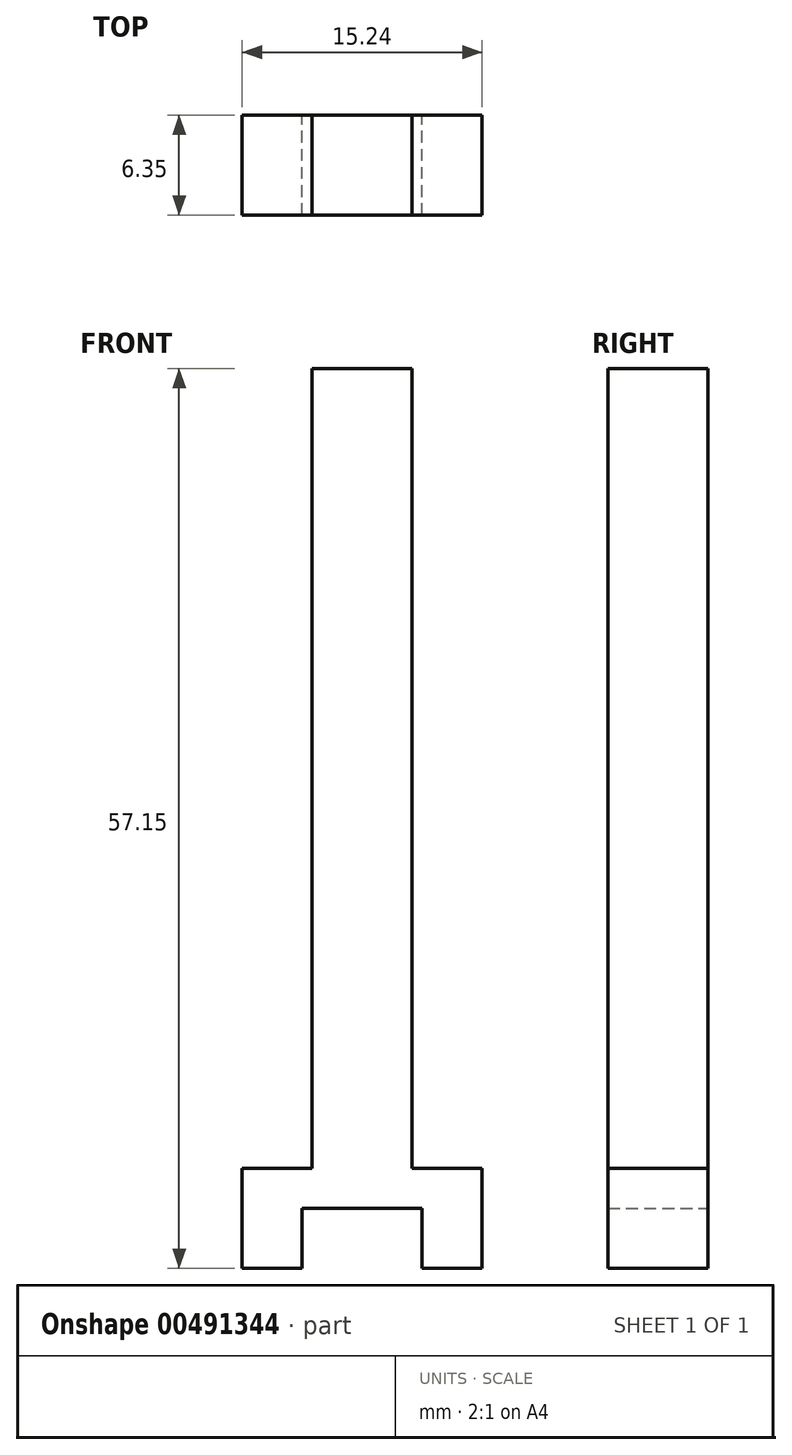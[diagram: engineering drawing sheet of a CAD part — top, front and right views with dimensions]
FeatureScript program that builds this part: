
annotation { "Feature Type Name" : "Feature", "Feature Type Description" : "" }
export const myFeature = defineFeature(function(context is Context, id is Id, definition is map)
    precondition{}
    {
        {
            var Q0;
            Q0=qCreatedBy(makeId("Front.planeOp"),FACE);
            var sketch = newSketch(context, id + "F0", { "sketchPlane" : qUnion([Q0])});
            skLineSegment(sketch, "E0.bottom", {"start": v(0, 0) * mm, "end": v(15.24, 0) * mm});
            skLineSegment(sketch, "E0.top", {"start": v(0, 6.35) * mm, "end": v(15.24, 6.35) * mm});
            skLineSegment(sketch, "E0.left", {"start": v(0, 0) * mm, "end": v(0, 6.35) * mm});
            skLineSegment(sketch, "E0.right", {"start": v(15.24, 0) * mm, "end": v(15.24, 6.35) * mm});
            skLineSegment(sketch, "E1.bottom", {"start": v(3.81, 0) * mm, "end": v(11.43, 0) * mm});
            skLineSegment(sketch, "E1.top", {"start": v(3.8, 3.81) * mm, "end": v(11.43, 3.81) * mm});
            skLineSegment(sketch, "E1.left", {"start": v(3.81, 0) * mm, "end": v(3.8, 3.8) * mm});
            skLineSegment(sketch, "E1.right", {"start": v(11.43, 0) * mm, "end": v(11.43, 3.8) * mm});
            skSolve(sketch);
        }
        {
            var Q0;
            Q0=makeQuery(id+"F0.imprint","IMPRINT",FACE,{"disambiguationData":[TD([[makeQuery(id+"F0.imprint","IMPRINT",EDGE,{"derivedFrom":sQuery(id+"F0.wireOp",EDGE,"E0.top")}),-1.0]])]});
            extrude(context, id + "F1", {"entities" : qUnion([Q0]), "depth" : 6.35 * mm});
        }
        {
            var Q0;
            Q0=makeQuery(id+"F1.opExtrude","SWEPT_FACE",FACE,{"disambiguationData":[OSD([sQuery(id+"F0.wireOp",EDGE,"E0.top")])]});
            var sketch = newSketch(context, id + "F2", { "sketchPlane" : qUnion([Q0])});
            skPoint(sketch, "E2.middle", {"position": v(7.3, -2.96) * mm});
            skLineSegment(sketch, "E3.bottom", {"start": v(4.44, 0) * mm, "end": v(10.8, 0) * mm});
            skLineSegment(sketch, "E3.top", {"start": v(4.44, -6.35) * mm, "end": v(10.8, -6.35) * mm});
            skLineSegment(sketch, "E3.left", {"start": v(4.44, 0) * mm, "end": v(4.44, -6.35) * mm});
            skLineSegment(sketch, "E3.right", {"start": v(10.8, 0) * mm, "end": v(10.8, -6.35) * mm});
            skSolve(sketch);
        }
        {
            var Q0;
            Q0=makeQuery(id+"F2.imprint","IMPRINT",FACE,{"disambiguationData":[TD([[makeQuery(id+"F2.imprint","IMPRINT",EDGE,{"derivedFrom":sQuery(id+"F2.wireOp",EDGE,"E3.bottom")}),-1.0]])]});
            extrude(context, id + "F3", {"entities" : qUnion([Q0]), "operationType" : NewBodyOperationType.ADD, "depth" : 50.8 * mm});
        }
    });
